# Revit family: RN 11000 Réducteur de pression sans raccords
name_source: partatom
category: Rohrzubehör
units: mm (PartAtom-declared; Revit-internal decimal feet)

## family parameters
Arbeitsebenenbasiert = Nein
Beim Laden mit Abzugskörper schneiden = Nein
Bemaßung runder Anschluss = Durchmesser verwenden
Gemeinsam genutzt = Nein
Immer vertikal = Ja
Teiletyp = Ventil - Zerlegung in

## types (7) — shared parameters
1.010.00.2 Blattnummer der Richtlinie = 17
1.010.00.3 Ausgabedatum (Monat) der Richtlinie = 201601
1.010.00.4 Herstellername = R. Nussbaum AG
1.010.00.5 Revisionsdatum der Datei = 20190528
1.010.00.6 Webadresse des Herstellers = http://www.nussbaum.ch
1.100.00.3 Sortiernummer für Anzeigereihenfolge = 8
1.100.00.4 Produktbezeichnung = Druckminderer
1.960/3L.00.8 Link (URL) = https://www.nussbaum.ch
17.700.00.4 Armaturentyp = 8
17.700.00.7 Maximale Betriebstemperatur TB [°C] = 30
17.700.00.8 Maximaler Betriebsdruck (Arbeitsdruck) ps [1.0 · 105 Pa] = 16
Connector Visibility = Nein
EnclosingSpace Visibility = Nein
Hersteller = R. Nussbauzm AG
URL = https://www.nussbaum.ch

## per-type parameters (varying)
- DN 15: 1.800.00.3 TGA-Nummer=00800100000000000000000000000200700000000000000001???00000; 1.810.00.3 Hersteller-Bestellnummer=11000.34; 1.810.00.4 DATANORM-Nummer=11000.34; 1.810.00.5 StLB-Nummer=613.153; 1.810.00.6 GTIN-Nummer=7612945712325; 17.700.00.30 Produktbeschreibung=11000.34, Druckreduzierventil ohne Verschraubungen, Einstellbereich 2 bis 6 bar,; 17.700.00.5 Nennweite DN=15; 17.700.00.6 kvs-Wert [m3/h]=3.48; CONNECTOR0_DIAMETER_dX_0r=15 mm  [stored 0.0492126 ft]; CONNECTOR0_dX_00=40 mm; CONNECTOR0_dX_01=31 mm; CONNECTOR0_ref_dX=40 mm; CONNECTOR1_DIAMETER_dX_0r=15 mm  [stored 0.0492126 ft]; CONNECTOR1_dX_00=31 mm; CONNECTOR1_dX_01=40 mm; CONNECTOR1_ref_dX=40 mm; Modell=11000.34; R. Nussbaum AG 11000.34 de Visibility=Ja; R. Nussbaum AG 11000.35 de Visibility=Nein; R. Nussbaum AG 11000.36 de Visibility=Nein; R. Nussbaum AG 11000.37 de Visibility=Nein; R. Nussbaum AG 11000.38 de Visibility=Nein; R. Nussbaum AG 11000.39 de Visibility=Nein; R. Nussbaum AG 11000.40 de Visibility=Nein; Typenkommentare=Réducteur de pression sans raccordsDN 15
- DN 20: 1.800.00.3 TGA-Nummer=00800100000000000000000000000200700000000000000002???00000; 1.810.00.3 Hersteller-Bestellnummer=11000.35; 1.810.00.4 DATANORM-Nummer=11000.35; 1.810.00.5 StLB-Nummer=613.154; 1.810.00.6 GTIN-Nummer=7612945712363; 17.700.00.30 Produktbeschreibung=11000.35, Druckreduzierventil ohne Verschraubungen, Einstellbereich 2 bis 6 bar,; 17.700.00.5 Nennweite DN=20; 17.700.00.6 kvs-Wert [m3/h]=4.5; CONNECTOR0_DIAMETER_dX_0r=20 mm  [stored 0.0656168 ft]; CONNECTOR0_dX_00=43 mm; CONNECTOR0_dX_01=34 mm; CONNECTOR0_ref_dX=43 mm; CONNECTOR1_DIAMETER_dX_0r=20 mm  [stored 0.0656168 ft]; CONNECTOR1_dX_00=34 mm; CONNECTOR1_dX_01=43 mm; CONNECTOR1_ref_dX=43 mm; Modell=11000.35; R. Nussbaum AG 11000.34 de Visibility=Nein; R. Nussbaum AG 11000.35 de Visibility=Ja; R. Nussbaum AG 11000.36 de Visibility=Nein; R. Nussbaum AG 11000.37 de Visibility=Nein; R. Nussbaum AG 11000.38 de Visibility=Nein; R. Nussbaum AG 11000.39 de Visibility=Nein; R. Nussbaum AG 11000.40 de Visibility=Nein; Typenkommentare=Réducteur de pression sans raccordsDN 20
- DN 25: 1.800.00.3 TGA-Nummer=00800100000000000000000000000200700000000000000003???00000; 1.810.00.3 Hersteller-Bestellnummer=11000.36; 1.810.00.4 DATANORM-Nummer=11000.36; 1.810.00.5 StLB-Nummer=613.155; 1.810.00.6 GTIN-Nummer=7612945712400; 17.700.00.30 Produktbeschreibung=11000.36, Druckreduzierventil ohne Verschraubungen, Einstellbereich 2 bis 6 bar,; 17.700.00.5 Nennweite DN=25; 17.700.00.6 kvs-Wert [m3/h]=5.52; CONNECTOR0_DIAMETER_dX_0r=25 mm  [stored 0.082021 ft]; CONNECTOR0_dX_00=50 mm  [stored 0.164042 ft]; CONNECTOR0_dX_01=38 mm; CONNECTOR0_ref_dX=50 mm  [stored 0.164042 ft]; CONNECTOR1_DIAMETER_dX_0r=25 mm  [stored 0.082021 ft]; CONNECTOR1_dX_00=38 mm; CONNECTOR1_dX_01=50 mm  [stored 0.164042 ft]; CONNECTOR1_ref_dX=50 mm  [stored 0.164042 ft]; Modell=11000.36; R. Nussbaum AG 11000.34 de Visibility=Nein; R. Nussbaum AG 11000.35 de Visibility=Nein; R. Nussbaum AG 11000.36 de Visibility=Ja; R. Nussbaum AG 11000.37 de Visibility=Nein; R. Nussbaum AG 11000.38 de Visibility=Nein; R. Nussbaum AG 11000.39 de Visibility=Nein; R. Nussbaum AG 11000.40 de Visibility=Nein; Typenkommentare=Réducteur de pression sans raccordsDN 25
- DN 32: 1.800.00.3 TGA-Nummer=00800100000000000000000000000200700000000000000004???00000; 1.810.00.3 Hersteller-Bestellnummer=11000.37; 1.810.00.4 DATANORM-Nummer=11000.37; 1.810.00.5 StLB-Nummer=613.156; 1.810.00.6 GTIN-Nummer=7612945711830; 17.700.00.30 Produktbeschreibung=11000.37, Druckreduzierventil ohne Verschraubungen, Einstellbereich 2 bis 6 bar,; 17.700.00.5 Nennweite DN=32; 17.700.00.6 kvs-Wert [m3/h]=13.2; CONNECTOR0_DIAMETER_dX_0r=32 mm  [stored 0.104987 ft]; CONNECTOR0_dX_00=60 mm; CONNECTOR0_dX_01=47 mm; CONNECTOR0_ref_dX=60 mm; CONNECTOR1_DIAMETER_dX_0r=32 mm  [stored 0.104987 ft]; CONNECTOR1_dX_00=47 mm; CONNECTOR1_dX_01=60 mm; CONNECTOR1_ref_dX=60 mm; Modell=11000.37; R. Nussbaum AG 11000.34 de Visibility=Nein; R. Nussbaum AG 11000.35 de Visibility=Nein; R. Nussbaum AG 11000.36 de Visibility=Nein; R. Nussbaum AG 11000.37 de Visibility=Ja; R. Nussbaum AG 11000.38 de Visibility=Nein; R. Nussbaum AG 11000.39 de Visibility=Nein; R. Nussbaum AG 11000.40 de Visibility=Nein; Typenkommentare=Réducteur de pression sans raccordsDN 32
- DN 40: 1.800.00.3 TGA-Nummer=00800100000000000000000000000200700000000000000005???00000; 1.810.00.3 Hersteller-Bestellnummer=11000.38; 1.810.00.4 DATANORM-Nummer=11000.38; 1.810.00.5 StLB-Nummer=613.157; 1.810.00.6 GTIN-Nummer=7612945711878; 17.700.00.30 Produktbeschreibung=11000.38, Druckreduzierventil ohne Verschraubungen, Einstellbereich 2 bis 6 bar,; 17.700.00.5 Nennweite DN=40; 17.700.00.6 kvs-Wert [m3/h]=16.2; CONNECTOR0_DIAMETER_dX_0r=40 mm; CONNECTOR0_dX_00=73 mm; CONNECTOR0_dX_01=59 mm; CONNECTOR0_ref_dX=73 mm; CONNECTOR1_DIAMETER_dX_0r=40 mm; CONNECTOR1_dX_00=59 mm; CONNECTOR1_dX_01=73 mm; CONNECTOR1_ref_dX=73 mm; Modell=11000.38; R. Nussbaum AG 11000.34 de Visibility=Nein; R. Nussbaum AG 11000.35 de Visibility=Nein; R. Nussbaum AG 11000.36 de Visibility=Nein; R. Nussbaum AG 11000.37 de Visibility=Nein; R. Nussbaum AG 11000.38 de Visibility=Ja; R. Nussbaum AG 11000.39 de Visibility=Nein; R. Nussbaum AG 11000.40 de Visibility=Nein; Typenkommentare=Réducteur de pression sans raccordsDN 40
- DN 50: 1.800.00.3 TGA-Nummer=00800100000000000000000000000200700000000000000006???00000; 1.810.00.3 Hersteller-Bestellnummer=11000.39; 1.810.00.4 DATANORM-Nummer=11000.39; 1.810.00.5 StLB-Nummer=613.158; 1.810.00.6 GTIN-Nummer=7612945712110; 17.700.00.30 Produktbeschreibung=11000.39, Druckreduzierventil ohne Verschraubungen, Einstellbereich 2 bis 6 bar,; 17.700.00.5 Nennweite DN=50; 17.700.00.6 kvs-Wert [m3/h]=21.6; CONNECTOR0_DIAMETER_dX_0r=50 mm  [stored 0.164042 ft]; CONNECTOR0_dX_00=88 mm; CONNECTOR0_dX_01=71 mm; CONNECTOR0_ref_dX=88 mm; CONNECTOR1_DIAMETER_dX_0r=50 mm  [stored 0.164042 ft]; CONNECTOR1_dX_00=71 mm; CONNECTOR1_dX_01=88 mm; CONNECTOR1_ref_dX=88 mm; Modell=11000.39; R. Nussbaum AG 11000.34 de Visibility=Nein; R. Nussbaum AG 11000.35 de Visibility=Nein; R. Nussbaum AG 11000.36 de Visibility=Nein; R. Nussbaum AG 11000.37 de Visibility=Nein; R. Nussbaum AG 11000.38 de Visibility=Nein; R. Nussbaum AG 11000.39 de Visibility=Ja; R. Nussbaum AG 11000.40 de Visibility=Nein; Typenkommentare=Réducteur de pression sans raccordsDN 50
- DN 65: 1.800.00.3 TGA-Nummer=00800100000000000000000000000200700000000000000007???00000; 1.810.00.3 Hersteller-Bestellnummer=11000.4; 1.810.00.4 DATANORM-Nummer=11000.4; 1.810.00.5 StLB-Nummer=613.161; 1.810.00.6 GTIN-Nummer=7612945713513; 17.700.00.30 Produktbeschreibung=11000.40, Druckreduzierventil ohne Verschraubungen, Einstellbereich 2 bis 6 bar,; 17.700.00.5 Nennweite DN=65; 17.700.00.6 kvs-Wert [m3/h]=44.4; CONNECTOR0_DIAMETER_dX_0r=65 mm  [stored 0.213255 ft]; CONNECTOR0_dX_00=145 mm; CONNECTOR0_dX_01=127 mm; CONNECTOR0_ref_dX=145 mm; CONNECTOR1_DIAMETER_dX_0r=65 mm  [stored 0.213255 ft]; CONNECTOR1_dX_00=127 mm; CONNECTOR1_dX_01=145 mm; CONNECTOR1_ref_dX=145 mm; Modell=11000.4; R. Nussbaum AG 11000.34 de Visibility=Nein; R. Nussbaum AG 11000.35 de Visibility=Nein; R. Nussbaum AG 11000.36 de Visibility=Nein; R. Nussbaum AG 11000.37 de Visibility=Nein; R. Nussbaum AG 11000.38 de Visibility=Nein; R. Nussbaum AG 11000.39 de Visibility=Nein; R. Nussbaum AG 11000.40 de Visibility=Ja; Typenkommentare=Réducteur de pression sans raccordsDN 65

note: [stored X ft] marks values corroborated as IEEE doubles in the binary element streams (Revit-internal decimal feet)

## geometry (parser evidence)
native form markers: Sweep x1
no freeform markers — native parametric forms only
